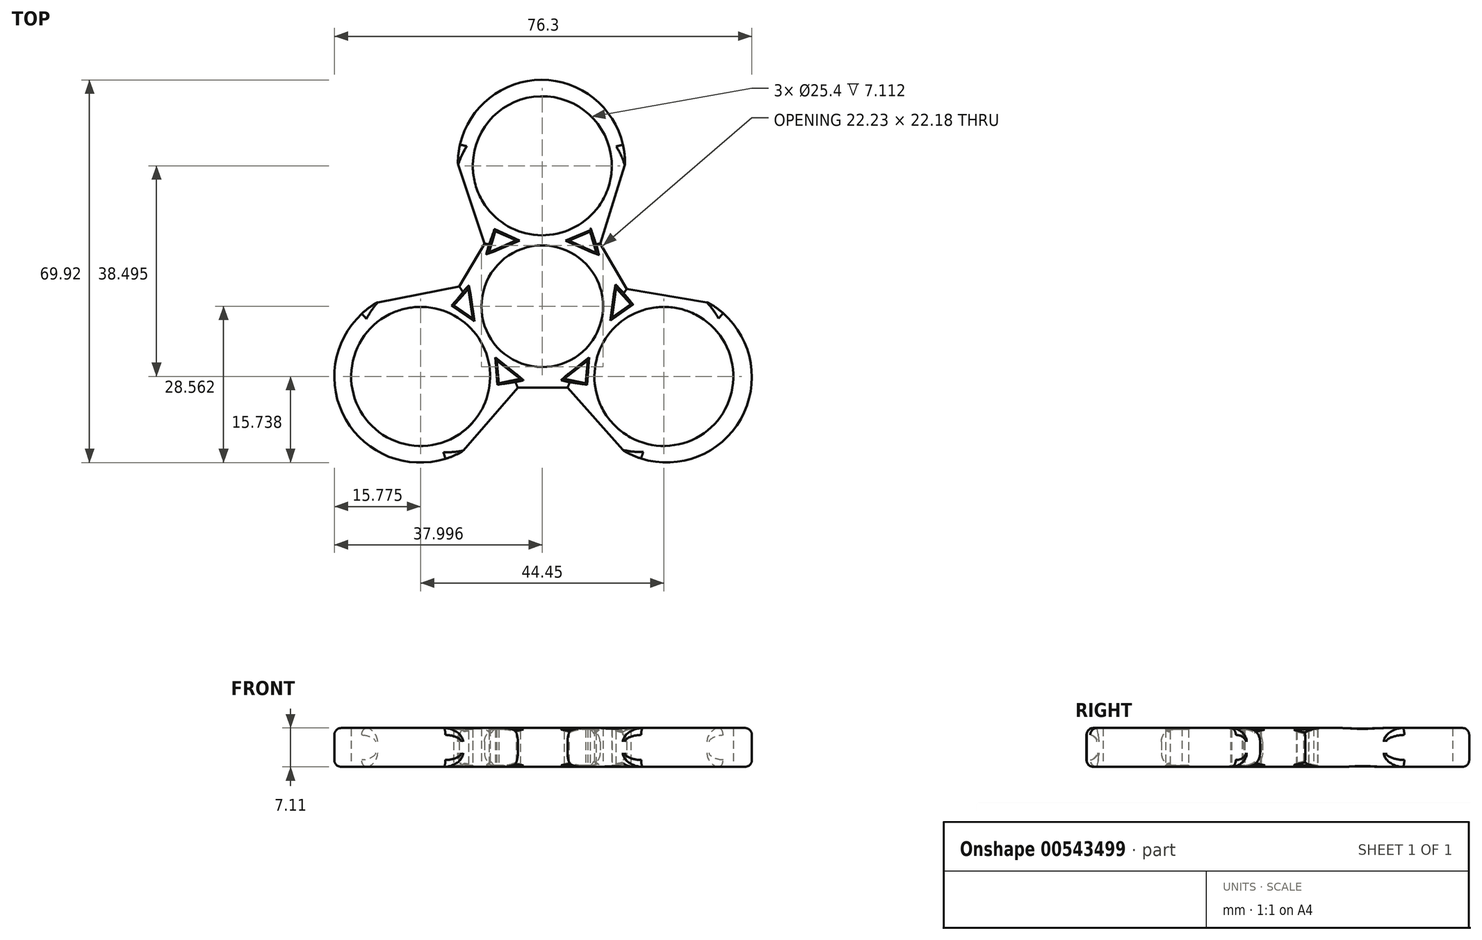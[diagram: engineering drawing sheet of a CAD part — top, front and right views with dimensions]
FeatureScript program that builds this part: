
annotation { "Feature Type Name" : "Feature", "Feature Type Description" : "" }
export const myFeature = defineFeature(function(context is Context, id is Id, definition is map)
    precondition{}
    {
        {
            var Q0;
            Q0=qCreatedBy(makeId("Top.planeOp"),FACE);
            var sketch = newSketch(context, id + "F0", { "sketchPlane" : qUnion([Q0])});
            skCircle(sketch, "E0", {"center": v(0, 0) * mm, "radius": 11.11 * mm});
            skCircle(sketch, "E1", {"center": v(0, 25.66) * mm, "radius": 12.7 * mm});
            skCircle(sketch, "E2", {"center": v(-22.23, -12.83) * mm, "radius": 12.7 * mm});
            skCircle(sketch, "E3", {"center": v(22.22, -12.83) * mm, "radius": 12.7 * mm});
            skArc(sketch, "E4", {"start": v(15.13, 25.91) * mm, "mid": v(-0.06, 41.35) * mm, "end": v(-15.42, 26.08) * mm});
            skLineSegment(sketch, "E5", {"start": v(-15.42, 26.08) * mm, "end": v(-10.57, 11.42) * mm});
            skLineSegment(sketch, "E6", {"start": v(-10.57, 11.42) * mm, "end": v(-15.42, 3.14) * mm});
            skPoint(sketch, "E7.trimOffspring.end.orphan", {"position": v(59.97, 25.66) * mm});
            skPoint(sketch, "E8.orphan", {"position": v(0, -43.7) * mm});
            skLineSegment(sketch, "E9.MirrorCS", {"start": v(10.57, 11.42) * mm, "end": v(15.42, 3.14) * mm});
            skLineSegment(sketch, "E10", {"start": v(-13.05, 0) * mm, "end": v(-11.11, 0) * mm});
            skLineSegment(sketch, "E11", {"start": v(0, 0) * mm, "end": v(0.33, -0.2) * mm});
            skLineSegment(sketch, "E12", {"start": v(0, 0) * mm, "end": v(-1.03, -0.6) * mm});
            skLineSegment(sketch, "E13.MirrorCS", {"start": v(-4.45, -14.9) * mm, "end": v(0.18, -14.9) * mm});
            skLineSegment(sketch, "E14.MirrorCS", {"start": v(-14.6, -26.55) * mm, "end": v(-4.45, -14.9) * mm});
            skLineSegment(sketch, "E15.MirrorCS", {"start": v(0.18, -14.9) * mm, "end": v(0, -14.9) * mm});
            skLineSegment(sketch, "E16.trimOffspring", {"start": v(-9.59, -5.62) * mm, "end": v(-9.6, -5.63) * mm});
            skLineSegment(sketch, "E17", {"start": v(-9.62, -5.56) * mm, "end": v(-9.63, -5.57) * mm});
            skLineSegment(sketch, "E18.MirrorCS", {"start": v(14.87, -26.42) * mm, "end": v(4.6, -14.88) * mm});
            skLineSegment(sketch, "E19.MirrorCS", {"start": v(-30.28, 0.64) * mm, "end": v(-15.13, 3.6) * mm});
            skArc(sketch, "E20", {"start": v(-30.28, 0.64) * mm, "mid": v(-35.9, -20.72) * mm, "end": v(-14.6, -26.55) * mm});
            skArc(sketch, "E21", {"start": v(14.87, -26.42) * mm, "mid": v(36.26, -20.68) * mm, "end": v(30.31, 0.65) * mm});
            skLineSegment(sketch, "E22", {"start": v(-8.57, 13.7) * mm, "end": v(-9.73, 9.86) * mm});
            skLineSegment(sketch, "E23", {"start": v(-9.73, 9.86) * mm, "end": v(-4.75, 12.02) * mm});
            skLineSegment(sketch, "E24", {"start": v(-4.75, 12.02) * mm, "end": v(-8.57, 13.7) * mm});
            skLineSegment(sketch, "E25.MirrorCS", {"start": v(4.9, 11.96) * mm, "end": v(8.75, 13.6) * mm});
            skLineSegment(sketch, "E26.MirrorCS", {"start": v(8.75, 13.6) * mm, "end": v(9.87, 9.74) * mm});
            skLineSegment(sketch, "E27.MirrorCS", {"start": v(9.87, 9.74) * mm, "end": v(4.9, 11.96) * mm});
            skLineSegment(sketch, "E28", {"start": v(-1.03, -0.6) * mm, "end": v(0.1, 0.04) * mm});
            skLineSegment(sketch, "E29", {"start": v(9.7, 5.43) * mm, "end": v(9.68, 5.42) * mm});
            skLineSegment(sketch, "E30.MirrorCS", {"start": v(-16.17, 0.16) * mm, "end": v(-13.5, 3.16) * mm});
            skCircle(sketch, "E31.MirrorC", {"center": v(0, -0.02) * mm, "radius": 11.11 * mm});
            skLineSegment(sketch, "E32.MirrorCS", {"start": v(-12.74, -2.22) * mm, "end": v(-16.17, 0.16) * mm});
            skLineSegment(sketch, "E33.MirrorCS", {"start": v(-13.5, 3.16) * mm, "end": v(-12.74, -2.22) * mm});
            skLineSegment(sketch, "E34.MirrorCS", {"start": v(-4.01, -13.28) * mm, "end": v(-8.3, -9.93) * mm});
            skLineSegment(sketch, "E35.MirrorCS", {"start": v(-7.95, -14.1) * mm, "end": v(-4.01, -13.28) * mm});
            skLineSegment(sketch, "E36.MirrorCS", {"start": v(-8.3, -9.93) * mm, "end": v(-7.95, -14.1) * mm});
            skLineSegment(sketch, "E37.MirrorCS", {"start": v(4.01, -13.28) * mm, "end": v(8.3, -9.93) * mm});
            skLineSegment(sketch, "E38.MirrorCS", {"start": v(8.3, -9.93) * mm, "end": v(7.95, -14.1) * mm});
            skLineSegment(sketch, "E39.MirrorCS", {"start": v(7.95, -14.1) * mm, "end": v(4.01, -13.28) * mm});
            skLineSegment(sketch, "E40.MirrorCS", {"start": v(16.19, 0.36) * mm, "end": v(13.47, 3.33) * mm});
            skLineSegment(sketch, "E41.MirrorCS", {"start": v(12.78, -2.06) * mm, "end": v(16.19, 0.36) * mm});
            skLineSegment(sketch, "E42.MirrorCS", {"start": v(13.47, 3.33) * mm, "end": v(12.78, -2.06) * mm});
            skPoint(sketch, "E43.MirrorCS.end.orphan", {"position": v(10.57, 11.42) * mm});
            skPoint(sketch, "E43.MirrorCS.start.orphan", {"position": v(15.42, 26.08) * mm});
            skLineSegment(sketch, "E44", {"start": v(15.13, 25.91) * mm, "end": v(10.57, 11.42) * mm});
            skPoint(sketch, "E45.MirrorCS.end.orphan", {"position": v(15.15, 3.6) * mm});
            skLineSegment(sketch, "E46", {"start": v(15.42, 3.14) * mm, "end": v(30.31, 0.65) * mm});
            skPoint(sketch, "E47.trimOffspring.end.orphan", {"position": v(-4.79, -15) * mm});
            skPoint(sketch, "E48.orphan", {"position": v(4.81, -14.8) * mm});
            skPoint(sketch, "E49.orphan", {"position": v(5.15, -14.88) * mm});
            skLineSegment(sketch, "E50", {"start": v(0.18, -14.9) * mm, "end": v(4.6, -14.88) * mm});
            skLineSegment(sketch, "E51.trimOffspring", {"start": v(0.07, 11.11) * mm, "end": v(0.07, 11.1) * mm});
            skPoint(sketch, "E52.orphan", {"position": v(0, 57.97) * mm});
            skPoint(sketch, "E53.MirrorCS.start.orphan", {"position": v(0.28, 46.67) * mm});
            skLineSegment(sketch, "E54.trimOffspring", {"start": v(0.1, 0.04) * mm, "end": v(0, -0.01) * mm});
            skLineSegment(sketch, "E55.trimOffspring", {"start": v(7.62, 8.06) * mm, "end": v(7.63, 8.08) * mm});
            skLineSegment(sketch, "E56.trimOffspring", {"start": v(9.47, 9.92) * mm, "end": v(9.74, 10.18) * mm});
            skPoint(sketch, "E57.orphan", {"position": v(13, 7.28) * mm});
            skLineSegment(sketch, "E58.trimOffspring", {"start": v(9.68, 5.42) * mm, "end": v(9.7, 5.43) * mm});
            skLineSegment(sketch, "E59.trimOffspring", {"start": v(-0.14, 0.29) * mm, "end": v(0.33, -0.2) * mm});
            skLineSegment(sketch, "E60.trimOffspring", {"start": v(0.01, 0.44) * mm, "end": v(0, -0.01) * mm});
            skLineSegment(sketch, "E61.trimOffspring", {"start": v(0.33, -0.2) * mm, "end": v(0, 0) * mm});
            skPoint(sketch, "E62.orphan", {"position": v(-62.83, 0) * mm});
            skLineSegment(sketch, "E63.trimOffspring", {"start": v(-0.43, 0) * mm, "end": v(0.14, 0) * mm});
            skLineSegment(sketch, "E64.trimOffspring", {"start": v(11.1, 0) * mm, "end": v(11.11, 0) * mm});
            skLineSegment(sketch, "E65.trimOffspring", {"start": v(7.94, -7.78) * mm, "end": v(7.94, -7.78) * mm});
            skLineSegment(sketch, "E66.trimOffspring", {"start": v(-0.28, 0.15) * mm, "end": v(0, -0.01) * mm});
            skPoint(sketch, "E67.start.orphan", {"position": v(-13, 7.28) * mm});
            skLineSegment(sketch, "E68.trimOffspring", {"start": v(-7.8, 7.92) * mm, "end": v(-7.8, 7.92) * mm});
            skLineSegment(sketch, "E69.trimOffspring", {"start": v(0, 0.43) * mm, "end": v(0, -0.02) * mm});
            skLineSegment(sketch, "E70.trimOffspring", {"start": v(0, -14.9) * mm, "end": v(0, -14.9) * mm});
            skLineSegment(sketch, "E71.trimOffspring", {"start": v(0, -11.11) * mm, "end": v(0, -11.13) * mm});
            skPoint(sketch, "E72.orphan", {"position": v(40.55, -23.13) * mm});
            skLineSegment(sketch, "E73.trimOffspring", {"start": v(-1.03, -0.6) * mm, "end": v(0.01, 0.44) * mm});
            skSolve(sketch);
        }
        {
            var Q0;
            {var subQ0=sQuery(id+"F0.wireOp",EDGE,"hbrwn88Y-5k96-OH8k-IYxf-GrKMP4LpuQhe");Q0=makeQuery(id+"F0.imprint","IMPRINT",FACE,{"disambiguationData":[TD([[makeQuery(id+"F0.imprint","IMPRINT",EDGE,{"derivedFrom":subQ0}),1.0]])]});}
            var Q1;
            {var subQ0=sQuery(id+"F0.wireOp",EDGE,"9e4539ac-2175-455a-be19-bfef757cac5c.trimOffspring");Q1=makeQuery(id+"F0.imprint","IMPRINT",FACE,{"disambiguationData":[TD([[makeQuery(id+"F0.imprint","IMPRINT",EDGE,{"derivedFrom":subQ0}),1.0]])]});}
            var Q2;
            {var subQ14=sQuery(id+"F0.wireOp",EDGE,"9e4539ac-2175-455a-be19-bfef757cac5c.trimOffspring");Q2=makeQuery(id+"F0.imprint","IMPRINT",FACE,{"disambiguationData":[TD([[makeQuery(id+"F0.imprint","IMPRINT",EDGE,{"derivedFrom":subQ14}),-1.0]])]});}
            var Q3;
            {var subQ13=sQuery(id+"F0.wireOp",EDGE,"hbrwn88Y-5k96-OH8k-IYxf-GrKMP4LpuQhe");Q3=makeQuery(id+"F0.imprint","IMPRINT",FACE,{"disambiguationData":[TD([[makeQuery(id+"F0.imprint","IMPRINT",EDGE,{"derivedFrom":subQ13}),-1.0]])]});}
            var Q4;
            {var subQ4=sQuery(id+"F0.wireOp",EDGE,"E67");var subQ6=sQuery(id+"F0.wireOp",EDGE,"E6");var subQ7=makeQuery(id+"F0.imprint","INTERSECT",VERTEX,{"derivedFrom":[subQ6,subQ4]});Q4=makeQuery(id+"F0.imprint","IMPRINT",FACE,{"disambiguationData":[TD([[makeQuery(id+"F0.imprint","IMPRINT",EDGE,{"disambiguationData":[TD([[subQ7,1.0]])],"derivedFrom":subQ6}),1.0]])]});}
            var Q5;
            {var subQ16=sQuery(id+"F0.wireOp",EDGE,"E30.MirrorCS");Q5=makeQuery(id+"F0.imprint","IMPRINT",FACE,{"disambiguationData":[TD([[makeQuery(id+"F0.imprint","IMPRINT",EDGE,{"derivedFrom":subQ16}),1.0]])]});}
            var Q6;
            {var subQ3=sQuery(id+"F0.wireOp",EDGE,"E2");var subQ10=sQuery(id+"F0.wireOp",EDGE,"E17");var subQ11=makeQuery(id+"F0.imprint","INTERSECT",VERTEX,{"derivedFrom":[subQ3,subQ10]});Q6=makeQuery(id+"F0.imprint","IMPRINT",FACE,{"disambiguationData":[TD([[makeQuery(id+"F0.imprint","IMPRINT",EDGE,{"disambiguationData":[TD([[subQ11,-1.0]])],"derivedFrom":subQ3}),-1.0]])]});}
            var Q7;
            {var subQ5=sQuery(id+"F0.wireOp",EDGE,"E14.MirrorCS");Q7=makeQuery(id+"F0.imprint","IMPRINT",FACE,{"disambiguationData":[TD([[makeQuery(id+"F0.imprint","IMPRINT",EDGE,{"derivedFrom":subQ5}),1.0]])]});}
            var Q8;
            {var subQ0=sQuery(id+"F0.wireOp",EDGE,"E18.MirrorCS");Q8=makeQuery(id+"F0.imprint","IMPRINT",FACE,{"disambiguationData":[TD([[makeQuery(id+"F0.imprint","IMPRINT",EDGE,{"derivedFrom":subQ0}),-1.0]])]});}
            var Q9;
            {var subQ0=sQuery(id+"F0.wireOp",EDGE,"E16.trimOffspring");var subQ1=sQuery(id+"F0.wireOp",EDGE,"E2");var subQ2=makeQuery(id+"F0.imprint","INTERSECT",VERTEX,{"derivedFrom":[subQ1,subQ0]});Q9=makeQuery(id+"F0.imprint","IMPRINT",FACE,{"disambiguationData":[TD([[makeQuery(id+"F0.imprint","IMPRINT",EDGE,{"disambiguationData":[TD([[subQ2,1.0]])],"derivedFrom":subQ1}),-1.0]])]});}
            var Q10;
            {var subQ0=sQuery(id+"F0.wireOp",EDGE,"E10");var subQ1=sQuery(id+"F0.wireOp",EDGE,"E0");var subQ2=makeQuery(id+"F0.imprint","INTERSECT",VERTEX,{"disambiguationData":[OD(0.0)],"derivedFrom":[subQ1,subQ0]});Q10=makeQuery(id+"F0.imprint","IMPRINT",FACE,{"disambiguationData":[TD([[makeQuery(id+"F0.imprint","IMPRINT",EDGE,{"disambiguationData":[TD([[subQ2,1.0]])],"derivedFrom":subQ1}),-1.0]])]});}
            var Q11;
            {var subQ0=sQuery(id+"F0.wireOp",EDGE,"zIACLTs2-RhEK-kR9S-6Kjw-XjQPEztwelbf");var subQ1=sQuery(id+"F0.wireOp",EDGE,"E3");var subQ2=makeQuery(id+"F0.imprint","INTERSECT",VERTEX,{"disambiguationData":[OD(0.0)],"derivedFrom":[subQ1,subQ0]});Q11=makeQuery(id+"F0.imprint","IMPRINT",FACE,{"disambiguationData":[TD([[makeQuery(id+"F0.imprint","IMPRINT",EDGE,{"disambiguationData":[TD([[subQ2,1.0]])],"derivedFrom":subQ1}),-1.0]])]});}
            var Q12;
            {var subQ0=sQuery(id+"F0.wireOp",EDGE,"zIACLTs2-RhEK-kR9S-6Kjw-XjQPEztwelbf");var subQ1=sQuery(id+"F0.wireOp",EDGE,"E3");var subQ2=makeQuery(id+"F0.imprint","INTERSECT",VERTEX,{"disambiguationData":[OD(1.0)],"derivedFrom":[subQ1,subQ0]});Q12=makeQuery(id+"F0.imprint","IMPRINT",FACE,{"disambiguationData":[TD([[makeQuery(id+"F0.imprint","IMPRINT",EDGE,{"disambiguationData":[TD([[subQ2,-1.0]])],"derivedFrom":subQ1}),-1.0]])]});}
            var Q13;
            {var subQ14=sQuery(id+"F0.wireOp",EDGE,"E40.MirrorCS");Q13=makeQuery(id+"F0.imprint","IMPRINT",FACE,{"disambiguationData":[TD([[makeQuery(id+"F0.imprint","IMPRINT",EDGE,{"derivedFrom":subQ14}),-1.0]])]});}
            var Q14;
            {var subQ7=sQuery(id+"F0.wireOp",EDGE,"E0");var subQ10=sQuery(id+"F0.wireOp",EDGE,"E29");var subQ12=makeQuery(id+"F0.imprint","INTERSECT",VERTEX,{"derivedFrom":[subQ7,subQ10]});Q14=makeQuery(id+"F0.imprint","IMPRINT",FACE,{"disambiguationData":[TD([[makeQuery(id+"F0.imprint","IMPRINT",EDGE,{"disambiguationData":[TD([[subQ12,-1.0]])],"derivedFrom":subQ7}),-1.0]])]});}
            extrude(context, id + "F1", {"entities" : qUnion([Q0, Q1, Q2, Q3, Q4, Q5, Q6, Q7, Q8, Q9, Q10, Q11, Q12, Q13, Q14]), "depth" : 7.11 * mm, "offsetDistance" : 25.4 * mm});
        }
        {
            var Q0;
            Q0=makeQuery(id+"F1.opExtrude","CAP_EDGE",EDGE,{"disambiguationData":[OSD([sQuery(id+"F0.wireOp",EDGE,"E5")])],"isStart":false});
            var Q1;
            Q1=makeQuery(id+"F1.opExtrude","CAP_EDGE",EDGE,{"disambiguationData":[OSD([sQuery(id+"F0.wireOp",EDGE,"E6")])],"isStart":false});
            var Q2;
            Q2=makeQuery(id+"F1.opExtrude","CAP_EDGE",EDGE,{"disambiguationData":[OSD([sQuery(id+"F0.wireOp",EDGE,"E19.MirrorCS")])],"isStart":false});
            var Q3;
            Q3=makeQuery(id+"F1.opExtrude","CAP_EDGE",EDGE,{"disambiguationData":[OSD([sQuery(id+"F0.wireOp",EDGE,"E14.MirrorCS")])],"isStart":false});
            var Q4;
            Q4=makeQuery(id+"F1.opExtrude","CAP_EDGE",EDGE,{"disambiguationData":[OSD([sQuery(id+"F0.wireOp",EDGE,"E13.MirrorCS")])],"isStart":false});
            var Q5;
            Q5=makeQuery(id+"F1.opExtrude","CAP_EDGE",EDGE,{"disambiguationData":[OSD([sQuery(id+"F0.wireOp",EDGE,"E50")])],"isStart":false});
            var Q6;
            Q6=makeQuery(id+"F1.opExtrude","CAP_EDGE",EDGE,{"disambiguationData":[OSD([sQuery(id+"F0.wireOp",EDGE,"E18.MirrorCS")])],"isStart":false});
            var Q7;
            Q7=makeQuery(id+"F1.opExtrude","CAP_EDGE",EDGE,{"disambiguationData":[OSD([sQuery(id+"F0.wireOp",EDGE,"E46")])],"isStart":false});
            var Q8;
            Q8=makeQuery(id+"F1.opExtrude","CAP_EDGE",EDGE,{"disambiguationData":[OSD([sQuery(id+"F0.wireOp",EDGE,"E9.MirrorCS")])],"isStart":false});
            var Q9;
            Q9=makeQuery(id+"F1.opExtrude","CAP_EDGE",EDGE,{"disambiguationData":[OSD([sQuery(id+"F0.wireOp",EDGE,"E44")])],"isStart":false});
            fillet(context, id + "F2", {"entities" : qUnion([Q0, Q1, Q2, Q3, Q4, Q5, Q6, Q7, Q8, Q9]), "radius" : 2.54 * mm, "tangentPropagation" : true, "allowEdgeOverflow" : false});
        }
        {
            var Q0;
            Q0=makeQuery(id+"F1.opExtrude","CAP_EDGE",EDGE,{"disambiguationData":[OSD([sQuery(id+"F0.wireOp",EDGE,"E44")])],"isStart":true});
            var Q1;
            Q1=makeQuery(id+"F1.opExtrude","CAP_EDGE",EDGE,{"disambiguationData":[OSD([sQuery(id+"F0.wireOp",EDGE,"E9.MirrorCS")])],"isStart":true});
            var Q2;
            Q2=makeQuery(id+"F1.opExtrude","CAP_EDGE",EDGE,{"disambiguationData":[OSD([sQuery(id+"F0.wireOp",EDGE,"E46")])],"isStart":true});
            var Q3;
            Q3=makeQuery(id+"F1.opExtrude","CAP_EDGE",EDGE,{"disambiguationData":[OSD([sQuery(id+"F0.wireOp",EDGE,"E18.MirrorCS")])],"isStart":true});
            var Q4;
            Q4=makeQuery(id+"F1.opExtrude","CAP_EDGE",EDGE,{"disambiguationData":[OSD([sQuery(id+"F0.wireOp",EDGE,"E50")])],"isStart":true});
            var Q5;
            Q5=makeQuery(id+"F1.opExtrude","CAP_EDGE",EDGE,{"disambiguationData":[OSD([sQuery(id+"F0.wireOp",EDGE,"E13.MirrorCS")])],"isStart":true});
            var Q6;
            Q6=makeQuery(id+"F1.opExtrude","CAP_EDGE",EDGE,{"disambiguationData":[OSD([sQuery(id+"F0.wireOp",EDGE,"E14.MirrorCS")])],"isStart":true});
            var Q7;
            Q7=makeQuery(id+"F1.opExtrude","CAP_EDGE",EDGE,{"disambiguationData":[OSD([sQuery(id+"F0.wireOp",EDGE,"E19.MirrorCS")])],"isStart":true});
            var Q8;
            Q8=makeQuery(id+"F1.opExtrude","CAP_EDGE",EDGE,{"disambiguationData":[OSD([sQuery(id+"F0.wireOp",EDGE,"E6")])],"isStart":true});
            var Q9;
            Q9=makeQuery(id+"F1.opExtrude","CAP_EDGE",EDGE,{"disambiguationData":[OSD([sQuery(id+"F0.wireOp",EDGE,"E5")])],"isStart":true});
            fillet(context, id + "F3", {"entities" : qUnion([Q0, Q1, Q2, Q3, Q4, Q5, Q6, Q7, Q8, Q9]), "radius" : 2.54 * mm, "tangentPropagation" : true, "allowEdgeOverflow" : false});
        }
        {
            var Q0;
            Q0=makeQuery(id+"F1.opExtrude","CAP_EDGE",EDGE,{"disambiguationData":[OSD([sQuery(id+"F0.wireOp",EDGE,"E21")])],"isStart":false});
            var Q1;
            Q1=makeQuery(id+"F1.opExtrude","CAP_EDGE",EDGE,{"disambiguationData":[OSD([sQuery(id+"F0.wireOp",EDGE,"E20")])],"isStart":false});
            var Q2;
            Q2=makeQuery(id+"F1.opExtrude","CAP_EDGE",EDGE,{"disambiguationData":[OSD([sQuery(id+"F0.wireOp",EDGE,"E4")])],"isStart":false});
            fillet(context, id + "F4", {"entities" : qUnion([Q0, Q1, Q2]), "radius" : 1.27 * mm, "tangentPropagation" : true, "allowEdgeOverflow" : false});
        }
        {
            var Q0;
            Q0=makeQuery(id+"F1.opExtrude","CAP_EDGE",EDGE,{"disambiguationData":[OSD([sQuery(id+"F0.wireOp",EDGE,"E23")])],"isStart":false});
            var Q1;
            Q1=makeQuery(id+"F1.opExtrude","CAP_EDGE",EDGE,{"disambiguationData":[OSD([sQuery(id+"F0.wireOp",EDGE,"E24")])],"isStart":false});
            var Q2;
            Q2=makeQuery(id+"F2.opFillet","BLEND_EDGE",EDGE,{"blendedFrom":[makeQuery(id+"F1.opExtrude","CAP_EDGE",EDGE,{"disambiguationData":[OSD([sQuery(id+"F0.wireOp",EDGE,"E5")])],"isStart":false}),makeQuery(id+"F1.opExtrude","SWEPT_FACE",FACE,{"disambiguationData":[OSD([sQuery(id+"F0.wireOp",EDGE,"E22")])]})],"blendedInto":[makeQuery(id+"F1.opExtrude","SWEPT_FACE",FACE,{"disambiguationData":[OSD([sQuery(id+"F0.wireOp",EDGE,"E22")])]})]});
            var Q3;
            Q3=makeQuery(id+"F2.opFillet","BLEND_EDGE",EDGE,{"blendedFrom":[makeQuery(id+"F1.opExtrude","CAP_EDGE",EDGE,{"disambiguationData":[OSD([sQuery(id+"F0.wireOp",EDGE,"E6")])],"isStart":false}),makeQuery(id+"F1.opExtrude","SWEPT_FACE",FACE,{"disambiguationData":[OSD([sQuery(id+"F0.wireOp",EDGE,"E23")])]})],"blendedInto":[makeQuery(id+"F1.opExtrude","SWEPT_FACE",FACE,{"disambiguationData":[OSD([sQuery(id+"F0.wireOp",EDGE,"E23")])]})]});
            var Q4;
            Q4=makeQuery(id+"F2.opFillet","BLEND_EDGE",EDGE,{"blendedFrom":[makeQuery(id+"F1.opExtrude","CAP_EDGE",EDGE,{"disambiguationData":[OSD([sQuery(id+"F0.wireOp",EDGE,"E6")])],"isStart":false}),makeQuery(id+"F1.opExtrude","SWEPT_FACE",FACE,{"disambiguationData":[OSD([sQuery(id+"F0.wireOp",EDGE,"E22")])]})],"blendedInto":[makeQuery(id+"F1.opExtrude","SWEPT_FACE",FACE,{"disambiguationData":[OSD([sQuery(id+"F0.wireOp",EDGE,"E22")])]})]});
            var Q5;
            Q5=makeQuery(id+"F1.opExtrude","CAP_EDGE",EDGE,{"disambiguationData":[OSD([sQuery(id+"F0.wireOp",EDGE,"E25.MirrorCS")])],"isStart":false});
            var Q6;
            Q6=makeQuery(id+"F2.opFillet","BLEND_EDGE",EDGE,{"blendedFrom":[makeQuery(id+"F1.opExtrude","CAP_EDGE",EDGE,{"disambiguationData":[OSD([sQuery(id+"F0.wireOp",EDGE,"E44")])],"isStart":false}),makeQuery(id+"F1.opExtrude","SWEPT_FACE",FACE,{"disambiguationData":[OSD([sQuery(id+"F0.wireOp",EDGE,"E26.MirrorCS")])]})],"blendedInto":[makeQuery(id+"F1.opExtrude","SWEPT_FACE",FACE,{"disambiguationData":[OSD([sQuery(id+"F0.wireOp",EDGE,"E26.MirrorCS")])]})]});
            var Q7;
            Q7=makeQuery(id+"F1.opExtrude","CAP_EDGE",EDGE,{"disambiguationData":[OSD([sQuery(id+"F0.wireOp",EDGE,"E27.MirrorCS")])],"isStart":false});
            var Q8;
            Q8=makeQuery(id+"F2.opFillet","BLEND_EDGE",EDGE,{"blendedFrom":[makeQuery(id+"F1.opExtrude","CAP_EDGE",EDGE,{"disambiguationData":[OSD([sQuery(id+"F0.wireOp",EDGE,"E9.MirrorCS")])],"isStart":false}),makeQuery(id+"F1.opExtrude","SWEPT_FACE",FACE,{"disambiguationData":[OSD([sQuery(id+"F0.wireOp",EDGE,"E27.MirrorCS")])]})],"blendedInto":[makeQuery(id+"F1.opExtrude","SWEPT_FACE",FACE,{"disambiguationData":[OSD([sQuery(id+"F0.wireOp",EDGE,"E27.MirrorCS")])]})]});
            var Q9;
            Q9=makeQuery(id+"F2.opFillet","BLEND_EDGE",EDGE,{"blendedFrom":[makeQuery(id+"F1.opExtrude","CAP_EDGE",EDGE,{"disambiguationData":[OSD([sQuery(id+"F0.wireOp",EDGE,"E9.MirrorCS")])],"isStart":false}),makeQuery(id+"F1.opExtrude","SWEPT_FACE",FACE,{"disambiguationData":[OSD([sQuery(id+"F0.wireOp",EDGE,"E26.MirrorCS")])]})],"blendedInto":[makeQuery(id+"F1.opExtrude","SWEPT_FACE",FACE,{"disambiguationData":[OSD([sQuery(id+"F0.wireOp",EDGE,"E26.MirrorCS")])]})]});
            var Q10;
            Q10=makeQuery(id+"F2.opFillet","BLEND_EDGE",EDGE,{"blendedFrom":[makeQuery(id+"F1.opExtrude","CAP_EDGE",EDGE,{"disambiguationData":[OSD([sQuery(id+"F0.wireOp",EDGE,"E46")])],"isStart":false}),makeQuery(id+"F1.opExtrude","SWEPT_FACE",FACE,{"disambiguationData":[OSD([sQuery(id+"F0.wireOp",EDGE,"E40.MirrorCS")])]})],"blendedInto":[makeQuery(id+"F1.opExtrude","SWEPT_FACE",FACE,{"disambiguationData":[OSD([sQuery(id+"F0.wireOp",EDGE,"E40.MirrorCS")])]})]});
            var Q11;
            Q11=makeQuery(id+"F2.opFillet","BLEND_EDGE",EDGE,{"blendedFrom":[makeQuery(id+"F1.opExtrude","CAP_EDGE",EDGE,{"disambiguationData":[OSD([sQuery(id+"F0.wireOp",EDGE,"E9.MirrorCS")])],"isStart":false}),makeQuery(id+"F1.opExtrude","SWEPT_FACE",FACE,{"disambiguationData":[OSD([sQuery(id+"F0.wireOp",EDGE,"E42.MirrorCS")])]})],"blendedInto":[makeQuery(id+"F1.opExtrude","SWEPT_FACE",FACE,{"disambiguationData":[OSD([sQuery(id+"F0.wireOp",EDGE,"E42.MirrorCS")])]})]});
            var Q12;
            Q12=makeQuery(id+"F1.opExtrude","CAP_EDGE",EDGE,{"disambiguationData":[OSD([sQuery(id+"F0.wireOp",EDGE,"E42.MirrorCS")])],"isStart":false});
            var Q13;
            Q13=makeQuery(id+"F1.opExtrude","CAP_EDGE",EDGE,{"disambiguationData":[OSD([sQuery(id+"F0.wireOp",EDGE,"E41.MirrorCS")])],"isStart":false});
            var Q14;
            Q14=makeQuery(id+"F1.opExtrude","CAP_EDGE",EDGE,{"disambiguationData":[OSD([sQuery(id+"F0.wireOp",EDGE,"E37.MirrorCS")])],"isStart":false});
            var Q15;
            Q15=makeQuery(id+"F1.opExtrude","CAP_EDGE",EDGE,{"disambiguationData":[OSD([sQuery(id+"F0.wireOp",EDGE,"E38.MirrorCS")])],"isStart":false});
            var Q16;
            Q16=makeQuery(id+"F2.opFillet","BLEND_EDGE",EDGE,{"blendedFrom":[makeQuery(id+"F1.opExtrude","CAP_EDGE",EDGE,{"disambiguationData":[OSD([sQuery(id+"F0.wireOp",EDGE,"E18.MirrorCS")])],"isStart":false}),makeQuery(id+"F1.opExtrude","SWEPT_FACE",FACE,{"disambiguationData":[OSD([sQuery(id+"F0.wireOp",EDGE,"E39.MirrorCS")])]})],"blendedInto":[makeQuery(id+"F1.opExtrude","SWEPT_FACE",FACE,{"disambiguationData":[OSD([sQuery(id+"F0.wireOp",EDGE,"E39.MirrorCS")])]})]});
            var Q17;
            Q17=makeQuery(id+"F2.opFillet","BLEND_EDGE",EDGE,{"blendedFrom":[makeQuery(id+"F1.opExtrude","CAP_EDGE",EDGE,{"disambiguationData":[OSD([sQuery(id+"F0.wireOp",EDGE,"E50")])],"isStart":false}),makeQuery(id+"F1.opExtrude","SWEPT_FACE",FACE,{"disambiguationData":[OSD([sQuery(id+"F0.wireOp",EDGE,"E37.MirrorCS")])]})],"blendedInto":[makeQuery(id+"F1.opExtrude","SWEPT_FACE",FACE,{"disambiguationData":[OSD([sQuery(id+"F0.wireOp",EDGE,"E37.MirrorCS")])]})]});
            var Q18;
            Q18=makeQuery(id+"F2.opFillet","BLEND_EDGE",EDGE,{"blendedFrom":[makeQuery(id+"F1.opExtrude","CAP_EDGE",EDGE,{"disambiguationData":[OSD([sQuery(id+"F0.wireOp",EDGE,"E50")])],"isStart":false}),makeQuery(id+"F1.opExtrude","SWEPT_FACE",FACE,{"disambiguationData":[OSD([sQuery(id+"F0.wireOp",EDGE,"E39.MirrorCS")])]})],"blendedInto":[makeQuery(id+"F1.opExtrude","SWEPT_FACE",FACE,{"disambiguationData":[OSD([sQuery(id+"F0.wireOp",EDGE,"E39.MirrorCS")])]})]});
            var Q19;
            Q19=makeQuery(id+"F1.opExtrude","CAP_EDGE",EDGE,{"disambiguationData":[OSD([sQuery(id+"F0.wireOp",EDGE,"E39.MirrorCS")])],"isStart":false});
            var Q20;
            Q20=makeQuery(id+"F1.opExtrude","CAP_EDGE",EDGE,{"disambiguationData":[OSD([sQuery(id+"F0.wireOp",EDGE,"E34.MirrorCS")])],"isStart":false});
            var Q21;
            Q21=makeQuery(id+"F1.opExtrude","CAP_EDGE",EDGE,{"disambiguationData":[OSD([sQuery(id+"F0.wireOp",EDGE,"E36.MirrorCS")])],"isStart":false});
            var Q22;
            Q22=makeQuery(id+"F2.opFillet","BLEND_EDGE",EDGE,{"blendedFrom":[makeQuery(id+"F1.opExtrude","CAP_EDGE",EDGE,{"disambiguationData":[OSD([sQuery(id+"F0.wireOp",EDGE,"E14.MirrorCS")])],"isStart":false}),makeQuery(id+"F1.opExtrude","SWEPT_FACE",FACE,{"disambiguationData":[OSD([sQuery(id+"F0.wireOp",EDGE,"E35.MirrorCS")])]})],"blendedInto":[makeQuery(id+"F1.opExtrude","SWEPT_FACE",FACE,{"disambiguationData":[OSD([sQuery(id+"F0.wireOp",EDGE,"E35.MirrorCS")])]})]});
            var Q23;
            Q23=makeQuery(id+"F2.opFillet","BLEND_EDGE",EDGE,{"blendedFrom":[makeQuery(id+"F1.opExtrude","CAP_EDGE",EDGE,{"disambiguationData":[OSD([sQuery(id+"F0.wireOp",EDGE,"E13.MirrorCS")])],"isStart":false}),makeQuery(id+"F1.opExtrude","SWEPT_FACE",FACE,{"disambiguationData":[OSD([sQuery(id+"F0.wireOp",EDGE,"E34.MirrorCS")])]})],"blendedInto":[makeQuery(id+"F1.opExtrude","SWEPT_FACE",FACE,{"disambiguationData":[OSD([sQuery(id+"F0.wireOp",EDGE,"E34.MirrorCS")])]})]});
            var Q24;
            Q24=makeQuery(id+"F2.opFillet","BLEND_EDGE",EDGE,{"blendedFrom":[makeQuery(id+"F1.opExtrude","CAP_EDGE",EDGE,{"disambiguationData":[OSD([sQuery(id+"F0.wireOp",EDGE,"E13.MirrorCS")])],"isStart":false}),makeQuery(id+"F1.opExtrude","SWEPT_FACE",FACE,{"disambiguationData":[OSD([sQuery(id+"F0.wireOp",EDGE,"E35.MirrorCS")])]})],"blendedInto":[makeQuery(id+"F1.opExtrude","SWEPT_FACE",FACE,{"disambiguationData":[OSD([sQuery(id+"F0.wireOp",EDGE,"E35.MirrorCS")])]})]});
            var Q25;
            Q25=makeQuery(id+"F1.opExtrude","CAP_EDGE",EDGE,{"disambiguationData":[OSD([sQuery(id+"F0.wireOp",EDGE,"E35.MirrorCS")])],"isStart":false});
            var Q26;
            Q26=makeQuery(id+"F1.opExtrude","CAP_EDGE",EDGE,{"disambiguationData":[OSD([sQuery(id+"F0.wireOp",EDGE,"E33.MirrorCS")])],"isStart":false});
            var Q27;
            Q27=makeQuery(id+"F2.opFillet","BLEND_EDGE",EDGE,{"blendedFrom":[makeQuery(id+"F1.opExtrude","CAP_EDGE",EDGE,{"disambiguationData":[OSD([sQuery(id+"F0.wireOp",EDGE,"E6")])],"isStart":false}),makeQuery(id+"F1.opExtrude","SWEPT_FACE",FACE,{"disambiguationData":[OSD([sQuery(id+"F0.wireOp",EDGE,"E33.MirrorCS")])]})],"blendedInto":[makeQuery(id+"F1.opExtrude","SWEPT_FACE",FACE,{"disambiguationData":[OSD([sQuery(id+"F0.wireOp",EDGE,"E33.MirrorCS")])]})]});
            var Q28;
            Q28=makeQuery(id+"F2.opFillet","BLEND_EDGE",EDGE,{"blendedFrom":[makeQuery(id+"F1.opExtrude","CAP_EDGE",EDGE,{"disambiguationData":[OSD([sQuery(id+"F0.wireOp",EDGE,"E19.MirrorCS")])],"isStart":false}),makeQuery(id+"F1.opExtrude","SWEPT_FACE",FACE,{"disambiguationData":[OSD([sQuery(id+"F0.wireOp",EDGE,"E30.MirrorCS")])]})],"blendedInto":[makeQuery(id+"F1.opExtrude","SWEPT_FACE",FACE,{"disambiguationData":[OSD([sQuery(id+"F0.wireOp",EDGE,"E30.MirrorCS")])]})]});
            var Q29;
            Q29=makeQuery(id+"F1.opExtrude","CAP_EDGE",EDGE,{"disambiguationData":[OSD([sQuery(id+"F0.wireOp",EDGE,"E32.MirrorCS")])],"isStart":false});
            var Q30;
            Q30=makeQuery(id+"F1.opExtrude","CAP_EDGE",EDGE,{"disambiguationData":[OSD([sQuery(id+"F0.wireOp",EDGE,"E30.MirrorCS")])],"isStart":false});
            var Q31;
            Q31=makeQuery(id+"F2.opFillet","BLEND_EDGE",EDGE,{"blendedFrom":[makeQuery(id+"F1.opExtrude","CAP_EDGE",EDGE,{"disambiguationData":[OSD([sQuery(id+"F0.wireOp",EDGE,"E6")])],"isStart":false}),makeQuery(id+"F1.opExtrude","SWEPT_FACE",FACE,{"disambiguationData":[OSD([sQuery(id+"F0.wireOp",EDGE,"E30.MirrorCS")])]})],"blendedInto":[makeQuery(id+"F1.opExtrude","SWEPT_FACE",FACE,{"disambiguationData":[OSD([sQuery(id+"F0.wireOp",EDGE,"E30.MirrorCS")])]})]});
            var Q32;
            Q32=makeQuery(id+"F2.opFillet","BLEND_EDGE",EDGE,{"blendedFrom":[makeQuery(id+"F1.opExtrude","CAP_EDGE",EDGE,{"disambiguationData":[OSD([sQuery(id+"F0.wireOp",EDGE,"E9.MirrorCS")])],"isStart":false}),makeQuery(id+"F1.opExtrude","SWEPT_FACE",FACE,{"disambiguationData":[OSD([sQuery(id+"F0.wireOp",EDGE,"E40.MirrorCS")])]})],"blendedInto":[makeQuery(id+"F1.opExtrude","SWEPT_FACE",FACE,{"disambiguationData":[OSD([sQuery(id+"F0.wireOp",EDGE,"E40.MirrorCS")])]})]});
            chamfer(context, id + "F5", {"entities" : qUnion([Q0, Q1, Q2, Q3, Q4, Q5, Q6, Q7, Q8, Q9, Q10, Q11, Q12, Q13, Q14, Q15, Q16, Q17, Q18, Q19, Q20, Q21, Q22, Q23, Q24, Q25, Q26, Q27, Q28, Q29, Q30, Q31, Q32]), "width" : 0.25 * mm, "tangentPropagation" : true});
        }
        {
            var Q0;
            Q0=makeQuery(id+"F3.opFillet","BLEND_EDGE",EDGE,{"blendedFrom":[makeQuery(id+"F1.opExtrude","CAP_EDGE",EDGE,{"disambiguationData":[OSD([sQuery(id+"F0.wireOp",EDGE,"E44")])],"isStart":true}),makeQuery(id+"F1.opExtrude","SWEPT_FACE",FACE,{"disambiguationData":[OSD([sQuery(id+"F0.wireOp",EDGE,"E26.MirrorCS")])]})],"blendedInto":[makeQuery(id+"F1.opExtrude","SWEPT_FACE",FACE,{"disambiguationData":[OSD([sQuery(id+"F0.wireOp",EDGE,"E26.MirrorCS")])]})]});
            var Q1;
            Q1=makeQuery(id+"F1.opExtrude","CAP_EDGE",EDGE,{"disambiguationData":[OSD([sQuery(id+"F0.wireOp",EDGE,"E25.MirrorCS")])],"isStart":true});
            var Q2;
            Q2=makeQuery(id+"F1.opExtrude","CAP_EDGE",EDGE,{"disambiguationData":[OSD([sQuery(id+"F0.wireOp",EDGE,"E27.MirrorCS")])],"isStart":true});
            var Q3;
            Q3=makeQuery(id+"F3.opFillet","BLEND_EDGE",EDGE,{"blendedFrom":[makeQuery(id+"F1.opExtrude","CAP_EDGE",EDGE,{"disambiguationData":[OSD([sQuery(id+"F0.wireOp",EDGE,"E9.MirrorCS")])],"isStart":true}),makeQuery(id+"F1.opExtrude","SWEPT_FACE",FACE,{"disambiguationData":[OSD([sQuery(id+"F0.wireOp",EDGE,"E27.MirrorCS")])]})],"blendedInto":[makeQuery(id+"F1.opExtrude","SWEPT_FACE",FACE,{"disambiguationData":[OSD([sQuery(id+"F0.wireOp",EDGE,"E27.MirrorCS")])]})]});
            var Q4;
            Q4=makeQuery(id+"F3.opFillet","BLEND_EDGE",EDGE,{"blendedFrom":[makeQuery(id+"F1.opExtrude","CAP_EDGE",EDGE,{"disambiguationData":[OSD([sQuery(id+"F0.wireOp",EDGE,"E9.MirrorCS")])],"isStart":true}),makeQuery(id+"F1.opExtrude","SWEPT_FACE",FACE,{"disambiguationData":[OSD([sQuery(id+"F0.wireOp",EDGE,"E26.MirrorCS")])]})],"blendedInto":[makeQuery(id+"F1.opExtrude","SWEPT_FACE",FACE,{"disambiguationData":[OSD([sQuery(id+"F0.wireOp",EDGE,"E26.MirrorCS")])]})]});
            var Q5;
            Q5=makeQuery(id+"F3.opFillet","BLEND_EDGE",EDGE,{"blendedFrom":[makeQuery(id+"F1.opExtrude","CAP_EDGE",EDGE,{"disambiguationData":[OSD([sQuery(id+"F0.wireOp",EDGE,"E46")])],"isStart":true}),makeQuery(id+"F1.opExtrude","SWEPT_FACE",FACE,{"disambiguationData":[OSD([sQuery(id+"F0.wireOp",EDGE,"E40.MirrorCS")])]})],"blendedInto":[makeQuery(id+"F1.opExtrude","SWEPT_FACE",FACE,{"disambiguationData":[OSD([sQuery(id+"F0.wireOp",EDGE,"E40.MirrorCS")])]})]});
            var Q6;
            Q6=makeQuery(id+"F3.opFillet","BLEND_EDGE",EDGE,{"blendedFrom":[makeQuery(id+"F1.opExtrude","CAP_EDGE",EDGE,{"disambiguationData":[OSD([sQuery(id+"F0.wireOp",EDGE,"E9.MirrorCS")])],"isStart":true}),makeQuery(id+"F1.opExtrude","SWEPT_FACE",FACE,{"disambiguationData":[OSD([sQuery(id+"F0.wireOp",EDGE,"E40.MirrorCS")])]})],"blendedInto":[makeQuery(id+"F1.opExtrude","SWEPT_FACE",FACE,{"disambiguationData":[OSD([sQuery(id+"F0.wireOp",EDGE,"E40.MirrorCS")])]})]});
            var Q7;
            Q7=makeQuery(id+"F1.opExtrude","CAP_EDGE",EDGE,{"disambiguationData":[OSD([sQuery(id+"F0.wireOp",EDGE,"E42.MirrorCS")])],"isStart":true});
            var Q8;
            Q8=makeQuery(id+"F1.opExtrude","CAP_EDGE",EDGE,{"disambiguationData":[OSD([sQuery(id+"F0.wireOp",EDGE,"E41.MirrorCS")])],"isStart":true});
            var Q9;
            Q9=makeQuery(id+"F1.opExtrude","CAP_EDGE",EDGE,{"disambiguationData":[OSD([sQuery(id+"F0.wireOp",EDGE,"E24")])],"isStart":true});
            var Q10;
            Q10=makeQuery(id+"F3.opFillet","BLEND_EDGE",EDGE,{"blendedFrom":[makeQuery(id+"F1.opExtrude","CAP_EDGE",EDGE,{"disambiguationData":[OSD([sQuery(id+"F0.wireOp",EDGE,"E5")])],"isStart":true}),makeQuery(id+"F1.opExtrude","SWEPT_FACE",FACE,{"disambiguationData":[OSD([sQuery(id+"F0.wireOp",EDGE,"E22")])]})],"blendedInto":[makeQuery(id+"F1.opExtrude","SWEPT_FACE",FACE,{"disambiguationData":[OSD([sQuery(id+"F0.wireOp",EDGE,"E22")])]})]});
            var Q11;
            Q11=makeQuery(id+"F3.opFillet","BLEND_EDGE",EDGE,{"blendedFrom":[makeQuery(id+"F1.opExtrude","CAP_EDGE",EDGE,{"disambiguationData":[OSD([sQuery(id+"F0.wireOp",EDGE,"E6")])],"isStart":true}),makeQuery(id+"F1.opExtrude","SWEPT_FACE",FACE,{"disambiguationData":[OSD([sQuery(id+"F0.wireOp",EDGE,"E22")])]})],"blendedInto":[makeQuery(id+"F1.opExtrude","SWEPT_FACE",FACE,{"disambiguationData":[OSD([sQuery(id+"F0.wireOp",EDGE,"E22")])]})]});
            var Q12;
            Q12=makeQuery(id+"F3.opFillet","BLEND_EDGE",EDGE,{"blendedFrom":[makeQuery(id+"F1.opExtrude","CAP_EDGE",EDGE,{"disambiguationData":[OSD([sQuery(id+"F0.wireOp",EDGE,"E6")])],"isStart":true}),makeQuery(id+"F1.opExtrude","SWEPT_FACE",FACE,{"disambiguationData":[OSD([sQuery(id+"F0.wireOp",EDGE,"E23")])]})],"blendedInto":[makeQuery(id+"F1.opExtrude","SWEPT_FACE",FACE,{"disambiguationData":[OSD([sQuery(id+"F0.wireOp",EDGE,"E23")])]})]});
            var Q13;
            Q13=makeQuery(id+"F1.opExtrude","CAP_EDGE",EDGE,{"disambiguationData":[OSD([sQuery(id+"F0.wireOp",EDGE,"E23")])],"isStart":true});
            var Q14;
            Q14=makeQuery(id+"F3.opFillet","BLEND_EDGE",EDGE,{"blendedFrom":[makeQuery(id+"F1.opExtrude","CAP_EDGE",EDGE,{"disambiguationData":[OSD([sQuery(id+"F0.wireOp",EDGE,"E19.MirrorCS")])],"isStart":true}),makeQuery(id+"F1.opExtrude","SWEPT_FACE",FACE,{"disambiguationData":[OSD([sQuery(id+"F0.wireOp",EDGE,"E30.MirrorCS")])]})],"blendedInto":[makeQuery(id+"F1.opExtrude","SWEPT_FACE",FACE,{"disambiguationData":[OSD([sQuery(id+"F0.wireOp",EDGE,"E30.MirrorCS")])]})]});
            var Q15;
            Q15=makeQuery(id+"F3.opFillet","BLEND_EDGE",EDGE,{"blendedFrom":[makeQuery(id+"F1.opExtrude","CAP_EDGE",EDGE,{"disambiguationData":[OSD([sQuery(id+"F0.wireOp",EDGE,"E6")])],"isStart":true}),makeQuery(id+"F1.opExtrude","SWEPT_FACE",FACE,{"disambiguationData":[OSD([sQuery(id+"F0.wireOp",EDGE,"E30.MirrorCS")])]})],"blendedInto":[makeQuery(id+"F1.opExtrude","SWEPT_FACE",FACE,{"disambiguationData":[OSD([sQuery(id+"F0.wireOp",EDGE,"E30.MirrorCS")])]})]});
            var Q16;
            Q16=makeQuery(id+"F3.opFillet","BLEND_EDGE",EDGE,{"blendedFrom":[makeQuery(id+"F1.opExtrude","CAP_EDGE",EDGE,{"disambiguationData":[OSD([sQuery(id+"F0.wireOp",EDGE,"E6")])],"isStart":true}),makeQuery(id+"F1.opExtrude","SWEPT_FACE",FACE,{"disambiguationData":[OSD([sQuery(id+"F0.wireOp",EDGE,"E33.MirrorCS")])]})],"blendedInto":[makeQuery(id+"F1.opExtrude","SWEPT_FACE",FACE,{"disambiguationData":[OSD([sQuery(id+"F0.wireOp",EDGE,"E33.MirrorCS")])]})]});
            var Q17;
            Q17=makeQuery(id+"F1.opExtrude","CAP_EDGE",EDGE,{"disambiguationData":[OSD([sQuery(id+"F0.wireOp",EDGE,"E33.MirrorCS")])],"isStart":true});
            var Q18;
            Q18=makeQuery(id+"F1.opExtrude","CAP_EDGE",EDGE,{"disambiguationData":[OSD([sQuery(id+"F0.wireOp",EDGE,"E32.MirrorCS")])],"isStart":true});
            var Q19;
            Q19=makeQuery(id+"F1.opExtrude","CAP_EDGE",EDGE,{"disambiguationData":[OSD([sQuery(id+"F0.wireOp",EDGE,"E30.MirrorCS")])],"isStart":true});
            var Q20;
            Q20=makeQuery(id+"F1.opExtrude","CAP_EDGE",EDGE,{"disambiguationData":[OSD([sQuery(id+"F0.wireOp",EDGE,"E34.MirrorCS")])],"isStart":true});
            var Q21;
            Q21=makeQuery(id+"F1.opExtrude","CAP_EDGE",EDGE,{"disambiguationData":[OSD([sQuery(id+"F0.wireOp",EDGE,"E36.MirrorCS")])],"isStart":true});
            var Q22;
            Q22=makeQuery(id+"F3.opFillet","BLEND_EDGE",EDGE,{"blendedFrom":[makeQuery(id+"F1.opExtrude","CAP_EDGE",EDGE,{"disambiguationData":[OSD([sQuery(id+"F0.wireOp",EDGE,"E14.MirrorCS")])],"isStart":true}),makeQuery(id+"F1.opExtrude","SWEPT_FACE",FACE,{"disambiguationData":[OSD([sQuery(id+"F0.wireOp",EDGE,"E35.MirrorCS")])]})],"blendedInto":[makeQuery(id+"F1.opExtrude","SWEPT_FACE",FACE,{"disambiguationData":[OSD([sQuery(id+"F0.wireOp",EDGE,"E35.MirrorCS")])]})]});
            var Q23;
            Q23=makeQuery(id+"F3.opFillet","BLEND_EDGE",EDGE,{"blendedFrom":[makeQuery(id+"F1.opExtrude","CAP_EDGE",EDGE,{"disambiguationData":[OSD([sQuery(id+"F0.wireOp",EDGE,"E13.MirrorCS")])],"isStart":true}),makeQuery(id+"F1.opExtrude","SWEPT_FACE",FACE,{"disambiguationData":[OSD([sQuery(id+"F0.wireOp",EDGE,"E34.MirrorCS")])]})],"blendedInto":[makeQuery(id+"F1.opExtrude","SWEPT_FACE",FACE,{"disambiguationData":[OSD([sQuery(id+"F0.wireOp",EDGE,"E34.MirrorCS")])]})]});
            var Q24;
            Q24=makeQuery(id+"F3.opFillet","BLEND_EDGE",EDGE,{"blendedFrom":[makeQuery(id+"F1.opExtrude","CAP_EDGE",EDGE,{"disambiguationData":[OSD([sQuery(id+"F0.wireOp",EDGE,"E13.MirrorCS")])],"isStart":true}),makeQuery(id+"F1.opExtrude","SWEPT_FACE",FACE,{"disambiguationData":[OSD([sQuery(id+"F0.wireOp",EDGE,"E35.MirrorCS")])]})],"blendedInto":[makeQuery(id+"F1.opExtrude","SWEPT_FACE",FACE,{"disambiguationData":[OSD([sQuery(id+"F0.wireOp",EDGE,"E35.MirrorCS")])]})]});
            var Q25;
            Q25=makeQuery(id+"F1.opExtrude","CAP_EDGE",EDGE,{"disambiguationData":[OSD([sQuery(id+"F0.wireOp",EDGE,"E35.MirrorCS")])],"isStart":true});
            var Q26;
            Q26=makeQuery(id+"F1.opExtrude","CAP_EDGE",EDGE,{"disambiguationData":[OSD([sQuery(id+"F0.wireOp",EDGE,"E37.MirrorCS")])],"isStart":true});
            var Q27;
            Q27=makeQuery(id+"F1.opExtrude","CAP_EDGE",EDGE,{"disambiguationData":[OSD([sQuery(id+"F0.wireOp",EDGE,"E38.MirrorCS")])],"isStart":true});
            var Q28;
            Q28=makeQuery(id+"F3.opFillet","BLEND_EDGE",EDGE,{"blendedFrom":[makeQuery(id+"F1.opExtrude","CAP_EDGE",EDGE,{"disambiguationData":[OSD([sQuery(id+"F0.wireOp",EDGE,"E18.MirrorCS")])],"isStart":true}),makeQuery(id+"F1.opExtrude","SWEPT_FACE",FACE,{"disambiguationData":[OSD([sQuery(id+"F0.wireOp",EDGE,"E39.MirrorCS")])]})],"blendedInto":[makeQuery(id+"F1.opExtrude","SWEPT_FACE",FACE,{"disambiguationData":[OSD([sQuery(id+"F0.wireOp",EDGE,"E39.MirrorCS")])]})]});
            var Q29;
            Q29=makeQuery(id+"F3.opFillet","BLEND_EDGE",EDGE,{"blendedFrom":[makeQuery(id+"F1.opExtrude","CAP_EDGE",EDGE,{"disambiguationData":[OSD([sQuery(id+"F0.wireOp",EDGE,"E50")])],"isStart":true}),makeQuery(id+"F1.opExtrude","SWEPT_FACE",FACE,{"disambiguationData":[OSD([sQuery(id+"F0.wireOp",EDGE,"E39.MirrorCS")])]})],"blendedInto":[makeQuery(id+"F1.opExtrude","SWEPT_FACE",FACE,{"disambiguationData":[OSD([sQuery(id+"F0.wireOp",EDGE,"E39.MirrorCS")])]})]});
            var Q30;
            Q30=makeQuery(id+"F3.opFillet","BLEND_EDGE",EDGE,{"blendedFrom":[makeQuery(id+"F1.opExtrude","CAP_EDGE",EDGE,{"disambiguationData":[OSD([sQuery(id+"F0.wireOp",EDGE,"E50")])],"isStart":true}),makeQuery(id+"F1.opExtrude","SWEPT_FACE",FACE,{"disambiguationData":[OSD([sQuery(id+"F0.wireOp",EDGE,"E37.MirrorCS")])]})],"blendedInto":[makeQuery(id+"F1.opExtrude","SWEPT_FACE",FACE,{"disambiguationData":[OSD([sQuery(id+"F0.wireOp",EDGE,"E37.MirrorCS")])]})]});
            var Q31;
            Q31=makeQuery(id+"F1.opExtrude","CAP_EDGE",EDGE,{"disambiguationData":[OSD([sQuery(id+"F0.wireOp",EDGE,"E39.MirrorCS")])],"isStart":true});
            var Q32;
            Q32=makeQuery(id+"F3.opFillet","BLEND_EDGE",EDGE,{"blendedFrom":[makeQuery(id+"F1.opExtrude","CAP_EDGE",EDGE,{"disambiguationData":[OSD([sQuery(id+"F0.wireOp",EDGE,"E9.MirrorCS")])],"isStart":true}),makeQuery(id+"F1.opExtrude","SWEPT_FACE",FACE,{"disambiguationData":[OSD([sQuery(id+"F0.wireOp",EDGE,"E42.MirrorCS")])]})],"blendedInto":[makeQuery(id+"F1.opExtrude","SWEPT_FACE",FACE,{"disambiguationData":[OSD([sQuery(id+"F0.wireOp",EDGE,"E42.MirrorCS")])]})]});
            chamfer(context, id + "F6", {"entities" : qUnion([Q0, Q1, Q2, Q3, Q4, Q5, Q6, Q7, Q8, Q9, Q10, Q11, Q12, Q13, Q14, Q15, Q16, Q17, Q18, Q19, Q20, Q21, Q22, Q23, Q24, Q25, Q26, Q27, Q28, Q29, Q30, Q31, Q32]), "width" : 0.25 * mm, "tangentPropagation" : true});
        }
    });
